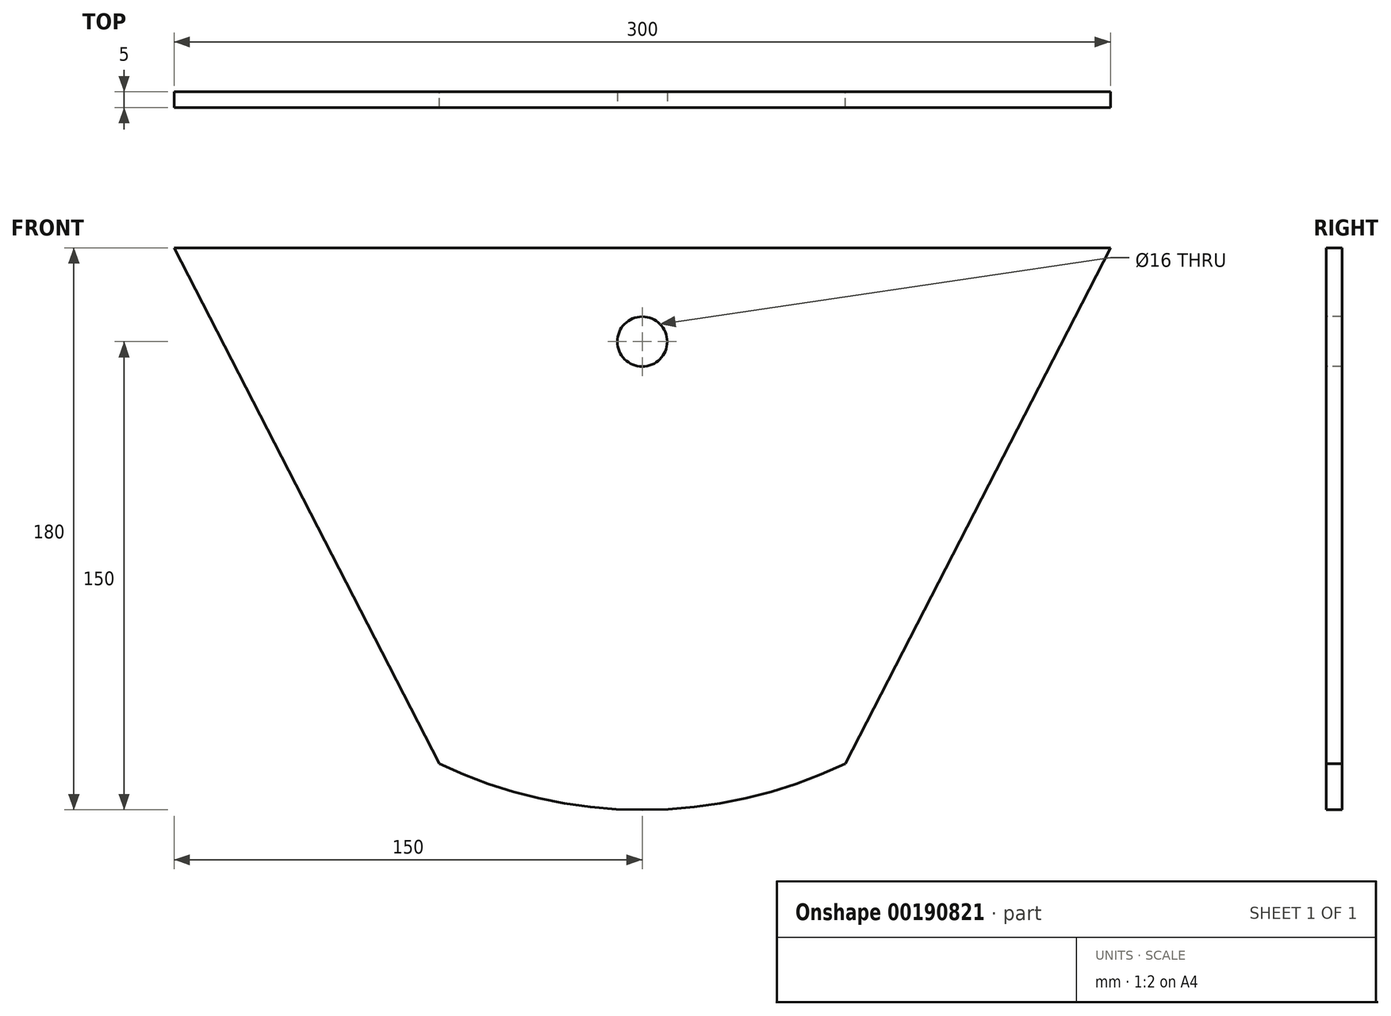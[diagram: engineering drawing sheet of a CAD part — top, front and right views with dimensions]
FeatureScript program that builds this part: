
annotation { "Feature Type Name" : "Feature", "Feature Type Description" : "" }
export const myFeature = defineFeature(function(context is Context, id is Id, definition is map)
    precondition{}
    {
        {
            var Q0;
            Q0=qCreatedBy(makeId("Front.planeOp"),FACE);
            var sketch = newSketch(context, id + "F0", { "sketchPlane" : qUnion([Q0])});
            skArc(sketch, "E0", {"start": v(-65, -135.19) * mm, "mid": v(0, -150) * mm, "end": v(65, -135.19) * mm});
            skLineSegment(sketch, "E1", {"start": v(65, -135.19) * mm, "end": v(150, 30) * mm});
            skLineSegment(sketch, "E2", {"start": v(-150, 30) * mm, "end": v(-65, -135.19) * mm});
            skLineSegment(sketch, "E3", {"start": v(-150, 30) * mm, "end": v(150, 30) * mm});
            skSolve(sketch);
        }
        {
            var Q0;
            Q0 = qSketchRegion(id + "F0", true);
            extrude(context, id + "F1", {"entities" : qUnion([Q0]), "depth" : 5 * mm});
        }
        {
            var Q0;
            Q0=makeQuery(id+"F1.opExtrude","CAP_FACE",FACE,{"disambiguationData":[OSD([sQuery(id+"F0.wireOp",EDGE,"E0"),sQuery(id+"F0.wireOp",EDGE,"E1"),sQuery(id+"F0.wireOp",EDGE,"E2"),sQuery(id+"F0.wireOp",EDGE,"E3")])],"isStart":false});
            var sketch = newSketch(context, id + "F2", { "sketchPlane" : qUnion([Q0])});
            skCircle(sketch, "E4", {"center": v(0, 0) * mm, "radius": 8 * mm});
            skSolve(sketch);
        }
        {
            var Q0;
            Q0 = qSketchRegion(id + "F2", true);
            extrude(context, id + "F3", {"entities" : qUnion([Q0]), "operationType" : NewBodyOperationType.REMOVE, "endBound" : BoundingType.THROUGH_ALL, "oppositeDirection" : true, "depth" : 25 * mm});
        }
    });
